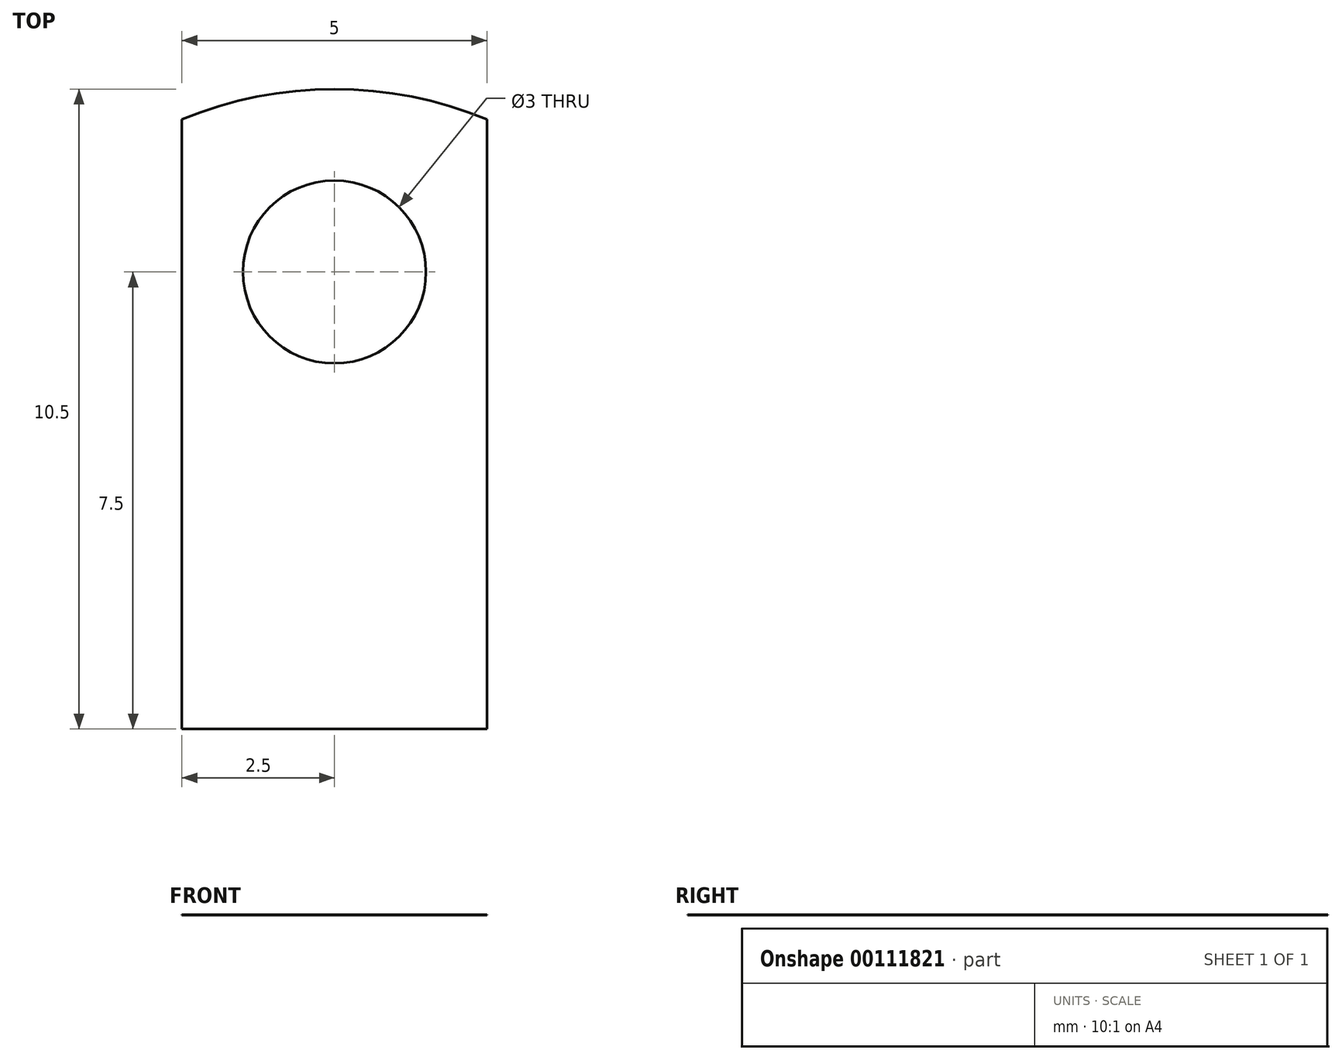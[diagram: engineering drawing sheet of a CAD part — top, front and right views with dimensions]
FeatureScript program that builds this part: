
annotation { "Feature Type Name" : "Feature", "Feature Type Description" : "" }
export const myFeature = defineFeature(function(context is Context, id is Id, definition is map)
    precondition{}
    {
        {
            var Q0;
            Q0=qCreatedBy(makeId("Top.planeOp"),FACE);
            var sketch = newSketch(context, id + "F0", { "sketchPlane" : qUnion([Q0])});
            skLineSegment(sketch, "E0.bottom", {"start": v(2.5, -5) * mm, "end": v(-2.5, -5) * mm});
            skLineSegment(sketch, "E0.left", {"start": v(2.5, -5) * mm, "end": v(2.5, 5) * mm});
            skLineSegment(sketch, "E0.right", {"start": v(-2.5, -5) * mm, "end": v(-2.5, 5) * mm});
            skPoint(sketch, "E0.middle", {"position": v(0, 0) * mm});
            skCircle(sketch, "E1", {"center": v(0, 2.5) * mm, "radius": 1.5 * mm});
            skArc(sketch, "E2", {"start": v(2.5, 5) * mm, "mid": v(0, 5.5) * mm, "end": v(-2.5, 5) * mm});
            skPoint(sketch, "E3", {"position": v(0, 5.5) * mm});
            skSolve(sketch);
        }
        {
            var Q0;
            Q0=makeQuery(id+"F0.imprint","IMPRINT",FACE,{"disambiguationData":[TD([[makeQuery(id+"F0.imprint","IMPRINT",EDGE,{"derivedFrom":sQuery(id+"F0.wireOp",EDGE,"E0.bottom")}),-1.0]])]});
            extrude(context, id + "F1", {"entities" : qUnion([Q0]), "depth" : 1 / 203.2 * mm});
        }
    });
